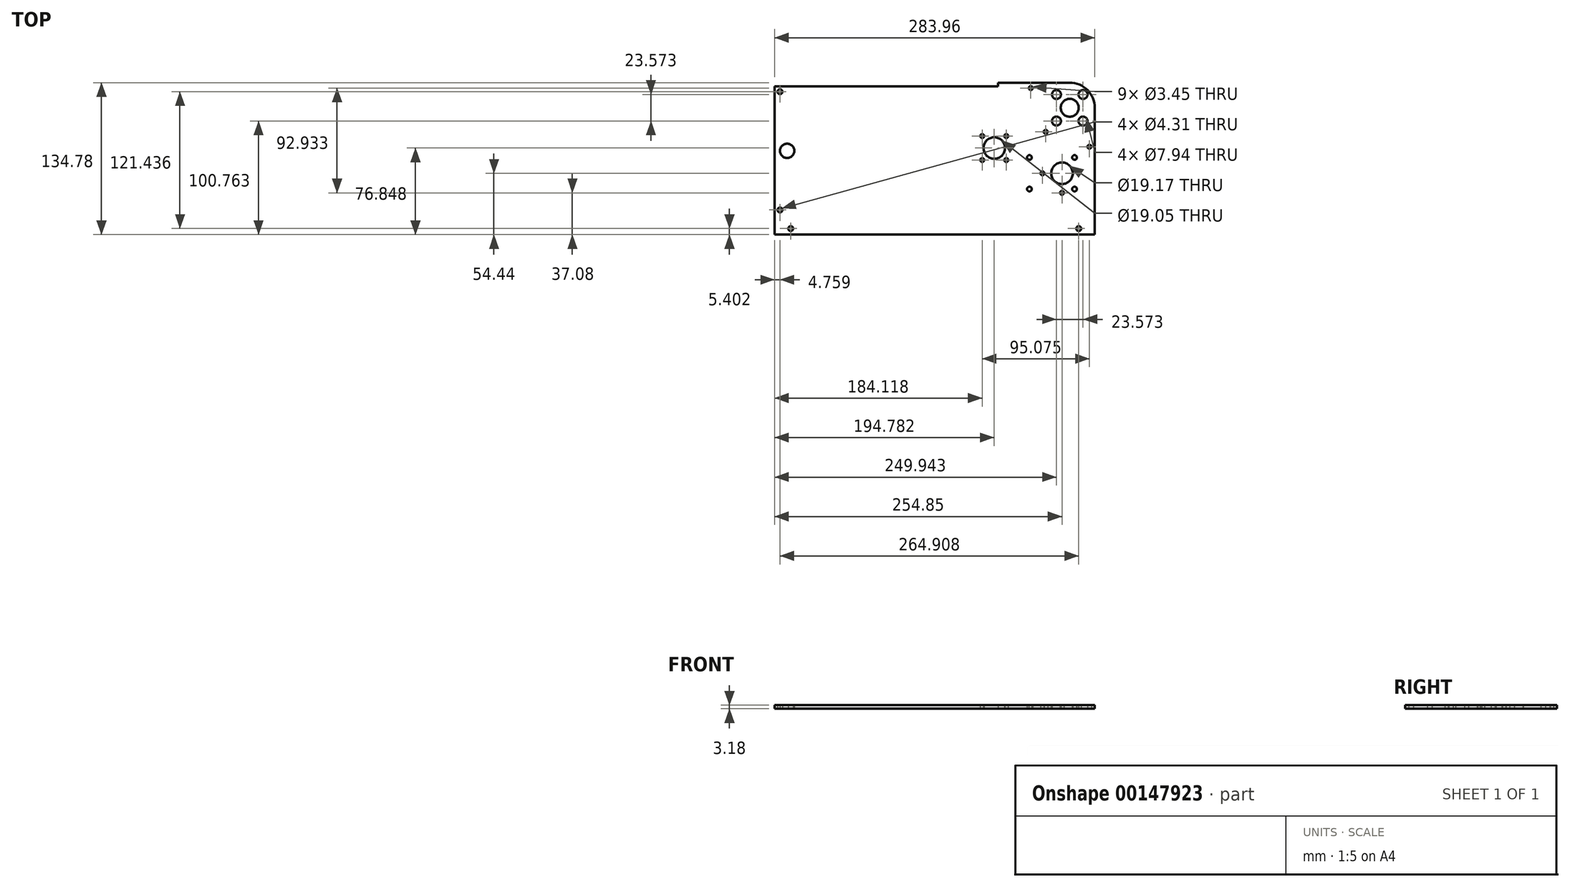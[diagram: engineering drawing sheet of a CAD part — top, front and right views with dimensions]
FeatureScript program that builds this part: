
annotation { "Feature Type Name" : "Feature", "Feature Type Description" : "" }
export const myFeature = defineFeature(function(context is Context, id is Id, definition is map)
    precondition{}
    {
        {
            var Q0;
            Q0=qCreatedBy(makeId("Top.planeOp"),FACE);
            var sketch = newSketch(context, id + "F0", { "sketchPlane" : qUnion([Q0])});
            skCircle(sketch, "E0", {"center": v(0, 0) * mm, "radius": 7.94 * mm});
            skLineSegment(sketch, "E1.bottom", {"start": v(-63.67, 22.23) * mm, "end": v(0, 22.23) * mm});
            skLineSegment(sketch, "E1.top", {"start": v(-261.73, -112.55) * mm, "end": v(22.23, -112.55) * mm});
            skLineSegment(sketch, "E1.left", {"start": v(-261.73, 19.05) * mm, "end": v(-261.73, -112.55) * mm});
            skArc(sketch, "E2", {"start": v(22.23, 0) * mm, "mid": v(15.72, 15.72) * mm, "end": v(0, 22.23) * mm});
            skLineSegment(sketch, "E3", {"start": v(22.23, -112.55) * mm, "end": v(22.23, -101.75) * mm});
            skLineSegment(sketch, "E4", {"start": v(22.23, -101.75) * mm, "end": v(22.23, 0) * mm});
            skLineSegment(sketch, "E5", {"start": v(0, 0) * mm, "end": v(0, -112.55) * mm, "construction": true});
            skLineSegment(sketch, "E6", {"start": v(22.23, -107.15) * mm, "end": v(7.94, -107.15) * mm, "construction": true});
            skCircle(sketch, "E7", {"center": v(7.94, -107.15) * mm, "radius": 2.15 * mm});
            skLineSegment(sketch, "E8", {"start": v(-261.73, -107.15) * mm, "end": v(-247.45, -107.15) * mm, "construction": true});
            skCircle(sketch, "E9", {"center": v(-247.45, -107.15) * mm, "radius": 2.15 * mm});
            skCircle(sketch, "E10", {"center": v(-256.97, 14.29) * mm, "radius": 2.15 * mm});
            skLineSegment(sketch, "E11", {"start": v(-256.97, 14.29) * mm, "end": v(-256.97, -90.64) * mm, "construction": true});
            skLineSegment(sketch, "E12", {"start": v(-256.97, -90.64) * mm, "end": v(-256.97, -107.15) * mm, "construction": true});
            skCircle(sketch, "E13", {"center": v(-256.97, -90.64) * mm, "radius": 2.15 * mm});
            skLineSegment(sketch, "E14.bottom", {"start": v(-35.73, -44.11) * mm, "end": v(4.27, -44.11) * mm, "construction": true});
            skLineSegment(sketch, "E14.top", {"start": v(-35.73, -72.11) * mm, "end": v(4.27, -72.11) * mm, "construction": true});
            skLineSegment(sketch, "E14.left", {"start": v(-35.73, -44.11) * mm, "end": v(-35.73, -72.11) * mm, "construction": true});
            skLineSegment(sketch, "E14.right", {"start": v(4.27, -44.11) * mm, "end": v(4.27, -72.11) * mm, "construction": true});
            skLineSegment(sketch, "E15", {"start": v(4.27, -58.11) * mm, "end": v(-6.88, -58.11) * mm, "construction": true});
            skCircle(sketch, "E16", {"center": v(-6.88, -58.11) * mm, "radius": 9.59 * mm});
            skCircle(sketch, "E17", {"center": v(-35.73, -44.11) * mm, "radius": 2.1 * mm});
            skCircle(sketch, "E18", {"center": v(-35.73, -72.11) * mm, "radius": 2.1 * mm});
            skCircle(sketch, "E19", {"center": v(4.27, -72.11) * mm, "radius": 2.1 * mm});
            skCircle(sketch, "E20", {"center": v(4.27, -44.11) * mm, "radius": 2.1 * mm});
            skLineSegment(sketch, "E21", {"start": v(0, 0) * mm, "end": v(-6.88, -58.11) * mm, "construction": true});
            skLineSegment(sketch, "E22", {"start": v(0, 0) * mm, "end": v(17.46, -34.55) * mm, "construction": true});
            skLineSegment(sketch, "E23", {"start": v(0, 0) * mm, "end": v(-34.55, 17.46) * mm, "construction": true});
            skLineSegment(sketch, "E24", {"start": v(0, 0) * mm, "end": v(-21.33, -21.33) * mm, "construction": true});
            skLineSegment(sketch, "E25", {"start": v(-21.33, -21.33) * mm, "end": v(17.46, -34.55) * mm, "construction": true});
            skLineSegment(sketch, "E26", {"start": v(-21.33, -21.33) * mm, "end": v(-34.55, 17.46) * mm, "construction": true});
            skCircle(sketch, "E27", {"center": v(-34.55, 17.46) * mm, "radius": 4.76 * mm, "construction": true});
            skCircle(sketch, "E28", {"center": v(-34.55, 17.46) * mm, "radius": 1.73 * mm});
            skCircle(sketch, "E29", {"center": v(-21.33, -21.33) * mm, "radius": 1.73 * mm});
            skCircle(sketch, "E30", {"center": v(17.46, -34.55) * mm, "radius": 1.73 * mm});
            skLineSegment(sketch, "E31", {"start": v(-256.97, 14.29) * mm, "end": v(-256.97, 19.05) * mm, "construction": true});
            skLineSegment(sketch, "E32", {"start": v(-256.97, 14.29) * mm, "end": v(-261.73, 14.29) * mm, "construction": true});
            skCircle(sketch, "E33", {"center": v(17.46, -34.55) * mm, "radius": 4.76 * mm, "construction": true});
            skLineSegment(sketch, "E34", {"start": v(-1.93, -27.94) * mm, "end": v(-3.47, -32.45) * mm, "construction": true});
            skLineSegment(sketch, "E35", {"start": v(15.93, -39.06) * mm, "end": v(-3.47, -32.45) * mm, "construction": true});
            skLineSegment(sketch, "E36.bottom", {"start": v(11.79, 11.79) * mm, "end": v(-11.79, 11.79) * mm, "construction": true});
            skLineSegment(sketch, "E36.top", {"start": v(11.79, -11.79) * mm, "end": v(-11.79, -11.79) * mm, "construction": true});
            skLineSegment(sketch, "E36.left", {"start": v(11.79, 11.79) * mm, "end": v(11.79, -11.79) * mm, "construction": true});
            skLineSegment(sketch, "E36.right", {"start": v(-11.79, 11.79) * mm, "end": v(-11.79, -11.79) * mm, "construction": true});
            skCircle(sketch, "E37", {"center": v(-11.79, 11.79) * mm, "radius": 3.97 * mm});
            skCircle(sketch, "E38", {"center": v(11.79, 11.79) * mm, "radius": 3.97 * mm});
            skCircle(sketch, "E39", {"center": v(11.79, -11.79) * mm, "radius": 3.97 * mm});
            skCircle(sketch, "E40", {"center": v(-11.79, -11.79) * mm, "radius": 3.97 * mm});
            skLineSegment(sketch, "E41", {"start": v(-256.97, -38.18) * mm, "end": v(-250.62, -38.18) * mm, "construction": true});
            skCircle(sketch, "E42", {"center": v(-250.62, -38.18) * mm, "radius": 6.35 * mm});
            skLineSegment(sketch, "E43.top", {"start": v(-63.67, 19.05) * mm, "end": v(-261.73, 19.05) * mm});
            skLineSegment(sketch, "E43.left", {"start": v(-63.67, 22.23) * mm, "end": v(-63.67, 19.05) * mm});
            skLineSegment(sketch, "E44", {"start": v(22.22, -35.7) * mm, "end": v(-66.95, -35.7) * mm, "construction": true});
            skLineSegment(sketch, "E45", {"start": v(-66.95, -35.7) * mm, "end": v(-66.95, -112.55) * mm, "construction": true});
            skCircle(sketch, "E46", {"center": v(-66.95, -35.7) * mm, "radius": 9.53 * mm});
            skCircle(sketch, "E47", {"center": v(-66.95, -35.7) * mm, "radius": 11.11 * mm, "construction": true});
            skCircle(sketch, "E48", {"center": v(-77.61, -46.37) * mm, "radius": 3.97 * mm, "construction": true});
            skCircle(sketch, "E49", {"center": v(-77.61, -25.04) * mm, "radius": 1.73 * mm});
            skCircle(sketch, "E50", {"center": v(-77.61, -46.37) * mm, "radius": 1.73 * mm});
            skLineSegment(sketch, "E51.bottom", {"start": v(-77.61, -46.37) * mm, "end": v(-56.28, -46.37) * mm, "construction": true});
            skLineSegment(sketch, "E51.top", {"start": v(-77.61, -25.04) * mm, "end": v(-56.28, -25.04) * mm, "construction": true});
            skLineSegment(sketch, "E51.left", {"start": v(-77.61, -46.37) * mm, "end": v(-77.61, -25.04) * mm, "construction": true});
            skLineSegment(sketch, "E51.right", {"start": v(-56.28, -46.37) * mm, "end": v(-56.28, -25.04) * mm, "construction": true});
            skCircle(sketch, "E52", {"center": v(-56.28, -25.04) * mm, "radius": 1.73 * mm});
            skCircle(sketch, "E53", {"center": v(-56.28, -46.37) * mm, "radius": 1.73 * mm});
            skLineSegment(sketch, "E54", {"start": v(-6.88, -58.11) * mm, "end": v(-15.56, -66.8) * mm, "construction": true});
            skLineSegment(sketch, "E55", {"start": v(-24.24, -58.11) * mm, "end": v(-6.88, -75.47) * mm, "construction": true});
            skLineSegment(sketch, "E56", {"start": v(-6.88, -58.11) * mm, "end": v(-6.88, -75.47) * mm, "construction": true});
            skCircle(sketch, "E57", {"center": v(-24.24, -58.11) * mm, "radius": 1.73 * mm});
            skCircle(sketch, "E58", {"center": v(-6.88, -75.47) * mm, "radius": 1.73 * mm});
            skSolve(sketch);
        }
        {
            var Q0;
            Q0=qSketchRegion(id+"F0",true);
            extrude(context, id + "F1", {"entities" : qUnion([Q0]), "depth" : 3.17 * mm});
        }
    });
